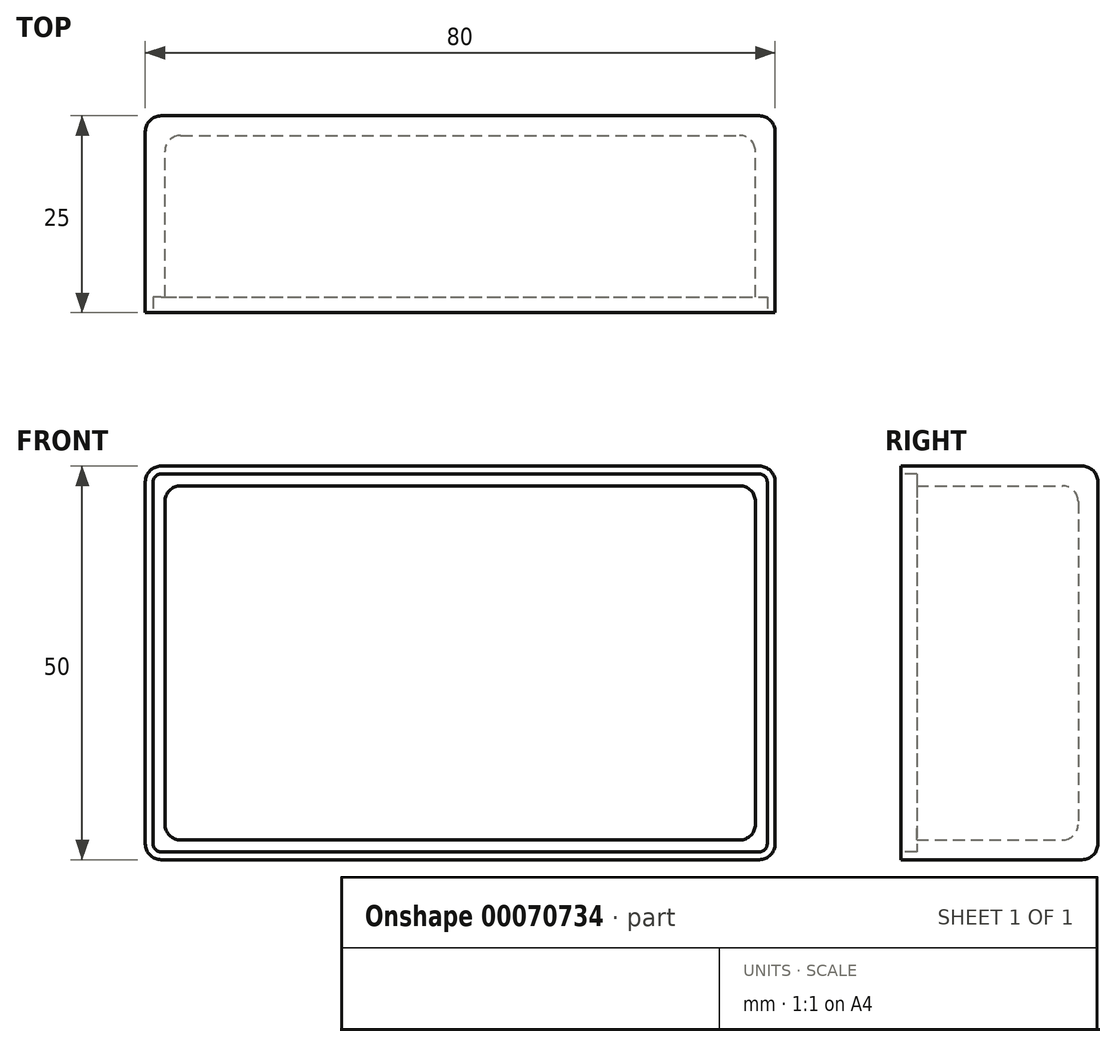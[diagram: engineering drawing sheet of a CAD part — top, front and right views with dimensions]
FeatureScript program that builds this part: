
annotation { "Feature Type Name" : "Feature", "Feature Type Description" : "" }
export const myFeature = defineFeature(function(context is Context, id is Id, definition is map)
    precondition{}
    {
        {
            var Q0;
            Q0=qCreatedBy(makeId("Front.planeOp"),FACE);
            var sketch = newSketch(context, id + "F0", { "sketchPlane" : qUnion([Q0])});
            skLineSegment(sketch, "E0.rect.bottom", {"start": v(-40, 25) * mm, "end": v(40, 25) * mm});
            skLineSegment(sketch, "E0.rect.top", {"start": v(-40, -25) * mm, "end": v(40, -25) * mm});
            skLineSegment(sketch, "E0.rect.left", {"start": v(-40, 25) * mm, "end": v(-40, -25) * mm});
            skLineSegment(sketch, "E0.rect.right", {"start": v(40, 25) * mm, "end": v(40, -25) * mm});
            skPoint(sketch, "E0.rect.middle", {"position": v(0, 0) * mm});
            skSolve(sketch);
        }
        {
            var Q0;
            Q0=makeQuery(id+"F0.imprint","IMPRINT",FACE,{"disambiguationData":[TD([[makeQuery(id+"F0.imprint","IMPRINT",EDGE,{"derivedFrom":sQuery(id+"F0.wireOp",EDGE,"E0.rect.bottom")}),-1.0]])]});
            extrude(context, id + "F1", {"entities" : qUnion([Q0]), "depth" : 25 * mm, "symmetric" : true});
        }
        {
            var Q0;
            Q0=makeQuery(id+"F1.opExtrude","CAP_FACE",FACE,{"disambiguationData":[OSD([sQuery(id+"F0.wireOp",EDGE,"E0.rect.bottom"),sQuery(id+"F0.wireOp",EDGE,"E0.rect.top"),sQuery(id+"F0.wireOp",EDGE,"E0.rect.left"),sQuery(id+"F0.wireOp",EDGE,"E0.rect.right")])],"isStart":false});
            shell(context, id + "F2", {"entities" : qUnion([Q0]), "thickness" : 2.5 * mm});
        }
        {
            var Q0;
            {var subQ0=sQuery(id+"F0.wireOp",EDGE,"E0.rect.right");Q0=makeQuery(id+"F2.opShell","OFFSET_EDGE",EDGE,{"disambiguationData":[OSD([subQ0]),TDD([makeQuery(id+"F1.opExtrude","CAP_EDGE",EDGE,{"disambiguationData":[OSD([subQ0])],"isStart":true})])]});}
            var Q1;
            {var subQ0=sQuery(id+"F0.wireOp",EDGE,"E0.rect.bottom");Q1=makeQuery(id+"F2.opShell","OFFSET_EDGE",EDGE,{"disambiguationData":[OSD([subQ0]),TDD([makeQuery(id+"F1.opExtrude","CAP_EDGE",EDGE,{"disambiguationData":[OSD([subQ0])],"isStart":true})])]});}
            var Q2;
            Q2=makeQuery(id+"F2.opShell","OFFSET_EDGE",EDGE,{"disambiguationData":[OSD([sQuery(id+"F0.wireOp",EDGE,"E0.rect.bottom"),sQuery(id+"F0.wireOp",EDGE,"E0.rect.right")])]});
            var Q3;
            Q3=makeQuery(id+"F2.opShell","OFFSET_EDGE",EDGE,{"disambiguationData":[OSD([sQuery(id+"F0.wireOp",EDGE,"E0.rect.top"),sQuery(id+"F0.wireOp",EDGE,"E0.rect.right")])]});
            var Q4;
            Q4=makeQuery(id+"F2.opShell","OFFSET_EDGE",EDGE,{"disambiguationData":[OSD([sQuery(id+"F0.wireOp",EDGE,"E0.rect.top"),sQuery(id+"F0.wireOp",EDGE,"E0.rect.left")])]});
            var Q5;
            {var subQ0=sQuery(id+"F0.wireOp",EDGE,"E0.rect.top");Q5=makeQuery(id+"F2.opShell","OFFSET_EDGE",EDGE,{"disambiguationData":[OSD([subQ0]),TDD([makeQuery(id+"F1.opExtrude","CAP_EDGE",EDGE,{"disambiguationData":[OSD([subQ0])],"isStart":true})])]});}
            var Q6;
            {var subQ0=sQuery(id+"F0.wireOp",EDGE,"E0.rect.left");Q6=makeQuery(id+"F2.opShell","OFFSET_EDGE",EDGE,{"disambiguationData":[OSD([subQ0]),TDD([makeQuery(id+"F1.opExtrude","CAP_EDGE",EDGE,{"disambiguationData":[OSD([subQ0])],"isStart":true})])]});}
            var Q7;
            Q7=makeQuery(id+"F2.opShell","OFFSET_EDGE",EDGE,{"disambiguationData":[OSD([sQuery(id+"F0.wireOp",EDGE,"E0.rect.bottom"),sQuery(id+"F0.wireOp",EDGE,"E0.rect.left")])]});
            fillet(context, id + "F3", {"entities" : qUnion([Q0, Q1, Q2, Q3, Q4, Q5, Q6, Q7]), "radius" : 2 * mm, "tangentPropagation" : true, "allowEdgeOverflow" : false});
        }
        {
            var Q0;
            Q0=makeQuery(id+"F1.opExtrude","CAP_FACE",FACE,{"disambiguationData":[OSD([sQuery(id+"F0.wireOp",EDGE,"E0.rect.bottom"),sQuery(id+"F0.wireOp",EDGE,"E0.rect.top"),sQuery(id+"F0.wireOp",EDGE,"E0.rect.left"),sQuery(id+"F0.wireOp",EDGE,"E0.rect.right")])],"isStart":true});
            var Q1;
            Q1=makeQuery(id+"F1.opExtrude","SWEPT_EDGE",EDGE,{"disambiguationData":[OSD([sQuery(id+"F0.wireOp",EDGE,"E0.rect.bottom"),sQuery(id+"F0.wireOp",EDGE,"E0.rect.left")])]});
            var Q2;
            Q2=makeQuery(id+"F1.opExtrude","SWEPT_EDGE",EDGE,{"disambiguationData":[OSD([sQuery(id+"F0.wireOp",EDGE,"E0.rect.bottom"),sQuery(id+"F0.wireOp",EDGE,"E0.rect.right")])]});
            var Q3;
            Q3=makeQuery(id+"F1.opExtrude","SWEPT_EDGE",EDGE,{"disambiguationData":[OSD([sQuery(id+"F0.wireOp",EDGE,"E0.rect.top"),sQuery(id+"F0.wireOp",EDGE,"E0.rect.left")])]});
            var Q4;
            Q4=makeQuery(id+"F1.opExtrude","SWEPT_EDGE",EDGE,{"disambiguationData":[OSD([sQuery(id+"F0.wireOp",EDGE,"E0.rect.top"),sQuery(id+"F0.wireOp",EDGE,"E0.rect.right")])]});
            fillet(context, id + "F4", {"entities" : qUnion([Q0, Q1, Q2, Q3, Q4]), "radius" : 2 * mm, "tangentPropagation" : true, "allowEdgeOverflow" : false});
        }
        {
            var Q0;
            Q0=makeQuery(id+"F1.opExtrude","CAP_FACE",FACE,{"disambiguationData":[OSD([sQuery(id+"F0.wireOp",EDGE,"E0.rect.bottom"),sQuery(id+"F0.wireOp",EDGE,"E0.rect.top"),sQuery(id+"F0.wireOp",EDGE,"E0.rect.left"),sQuery(id+"F0.wireOp",EDGE,"E0.rect.right")])],"isStart":false});
            var sketch = newSketch(context, id + "F5", { "sketchPlane" : qUnion([Q0])});
            skArc(sketch, "E1.0", {"start": v(-38, 24) * mm, "mid": v(-38.7, 23.7) * mm, "end": v(-39, 23) * mm});
            skLineSegment(sketch, "E1.1", {"start": v(-39, 23) * mm, "end": v(-39, -23) * mm});
            skLineSegment(sketch, "E1.2", {"start": v(-38, 24) * mm, "end": v(38, 24) * mm});
            skArc(sketch, "E1.3", {"start": v(-39, -23) * mm, "mid": v(-38.7, -23.7) * mm, "end": v(-38, -24) * mm});
            skArc(sketch, "E1.4", {"start": v(39, 23) * mm, "mid": v(38.7, 23.7) * mm, "end": v(38, 24) * mm});
            skLineSegment(sketch, "E1.5", {"start": v(39, 23) * mm, "end": v(39, -23) * mm});
            skArc(sketch, "E1.6", {"start": v(38, -24) * mm, "mid": v(38.7, -23.7) * mm, "end": v(39, -23) * mm});
            skLineSegment(sketch, "E1.7", {"start": v(-38, -24) * mm, "end": v(38, -24) * mm});
            skSolve(sketch);
        }
        {
            var Q0;
            Q0 = qSketchRegion(id + "F5", true);
            extrude(context, id + "F6", {"entities" : qUnion([Q0]), "operationType" : NewBodyOperationType.REMOVE, "oppositeDirection" : true, "depth" : 2 * mm});
        }
    });
